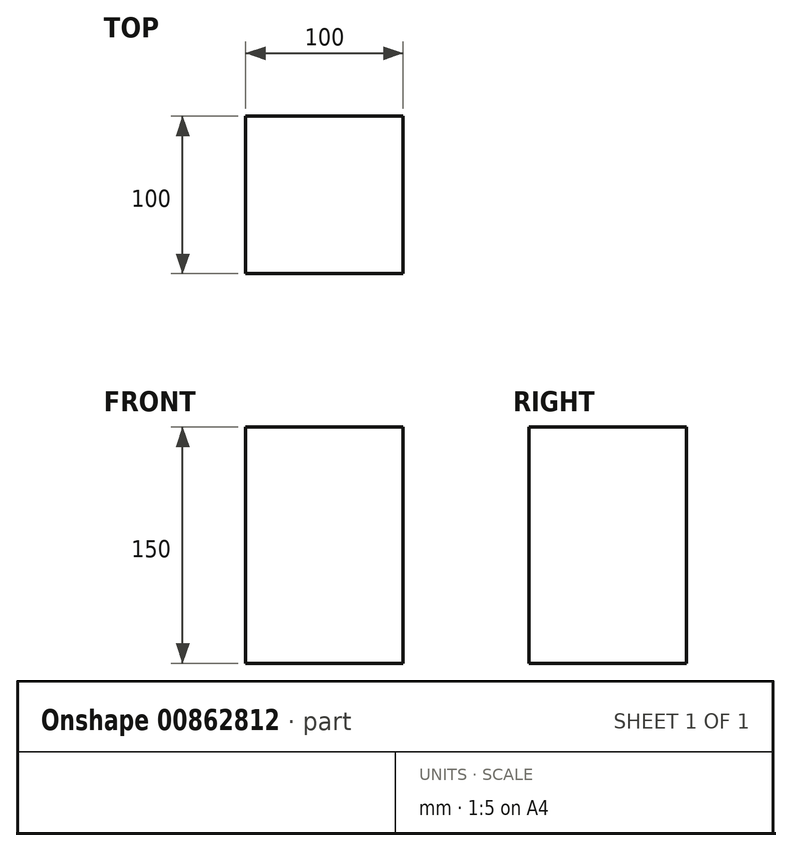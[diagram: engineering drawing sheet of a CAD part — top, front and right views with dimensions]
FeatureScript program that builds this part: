
annotation { "Feature Type Name" : "Feature", "Feature Type Description" : "" }
export const myFeature = defineFeature(function(context is Context, id is Id, definition is map)
    precondition{}
    {
        {
            var Q0;
            Q0=qCreatedBy(makeId("Top.planeOp"),FACE);
            var sketch = newSketch(context, id + "F0", { "sketchPlane" : qUnion([Q0])});
            skLineSegment(sketch, "E0.bottom", {"start": v(-50, 50) * mm, "end": v(50, 50) * mm});
            skLineSegment(sketch, "E0.top", {"start": v(-50, -50) * mm, "end": v(50, -50) * mm});
            skLineSegment(sketch, "E0.left", {"start": v(-50, 50) * mm, "end": v(-50, -50) * mm});
            skLineSegment(sketch, "E0.right", {"start": v(50, 50) * mm, "end": v(50, -50) * mm});
            skPoint(sketch, "E0.middle", {"position": v(0, 0) * mm});
            skSolve(sketch);
        }
        {
            var Q0;
            Q0=makeQuery(id+"F0.imprint","IMPRINT",FACE,{"disambiguationData":[TD([[makeQuery(id+"F0.imprint","IMPRINT",EDGE,{"derivedFrom":sQuery(id+"F0.wireOp",EDGE,"E0.bottom")}),-1.0]])]});
            extrude(context, id + "F1", {"entities" : qUnion([Q0]), "depth" : 150 * mm, "offsetDistance" : 25 * mm});
        }
    });
